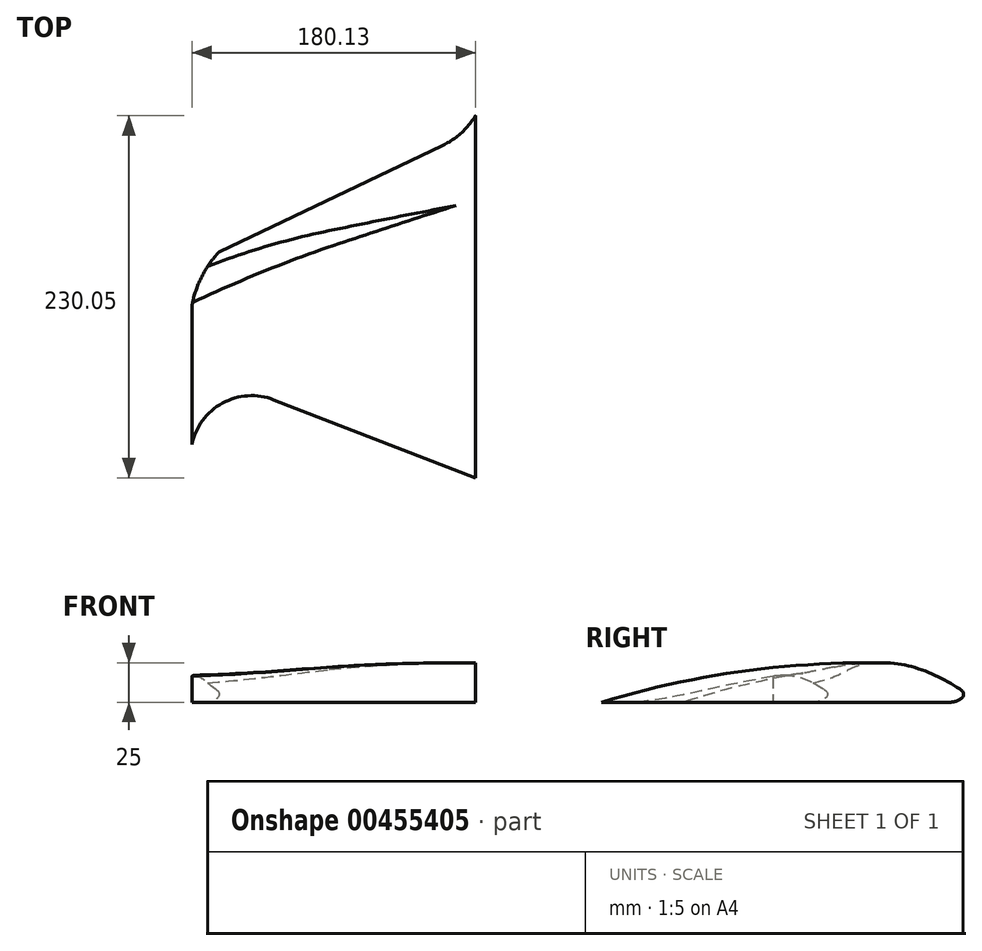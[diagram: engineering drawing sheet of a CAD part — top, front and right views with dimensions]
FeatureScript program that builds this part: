
annotation { "Feature Type Name" : "Feature", "Feature Type Description" : "" }
export const myFeature = defineFeature(function(context is Context, id is Id, definition is map)
    precondition{}
    {
        {
            var Q0;
            Q0=qCreatedBy(makeId("Top.planeOp"),FACE);
            var sketch = newSketch(context, id + "F0", { "sketchPlane" : qUnion([Q0])});
            skLineSegment(sketch, "E0", {"start": v(35.75, 56.99) * mm, "end": v(-84, 0) * mm});
            skArc(sketch, "E1", {"start": v(-84, 0) * mm, "mid": v(-108.74, -20.11) * mm, "end": v(-121.49, -49.34) * mm});
            skLineSegment(sketch, "E2", {"start": v(-121.49, -137.07) * mm, "end": v(-121.49, -49.34) * mm});
            skPoint(sketch, "E3.end.orphan", {"position": v(-24.95, -49.34) * mm});
            skArc(sketch, "E4", {"start": v(35.75, 56.99) * mm, "mid": v(49.78, 67.5) * mm, "end": v(58.64, 82.63) * mm});
            skLineSegment(sketch, "E5", {"start": v(58.64, -158.26) * mm, "end": v(58.64, 82.63) * mm});
            skLineSegment(sketch, "E6", {"start": v(-69.44, -108.67) * mm, "end": v(58.64, -158.26) * mm});
            skArc(sketch, "E7", {"start": v(-69.44, -108.67) * mm, "mid": v(-102.05, -110.8) * mm, "end": v(-121.49, -137.07) * mm});
            skSolve(sketch);
        }
        {
            var Q0;
            Q0=makeQuery(id+"F0.imprint","IMPRINT",FACE,{"disambiguationData":[TD([[makeQuery(id+"F0.imprint","IMPRINT",EDGE,{"derivedFrom":sQuery(id+"F0.wireOp",EDGE,"E0")}),1.0]])]});
            extrude(context, id + "F1", {"entities" : qUnion([Q0]), "depth" : 25 * mm});
        }
        {
            var Q0;
            Q0=makeQuery(id+"F1.opExtrude","CAP_EDGE",EDGE,{"disambiguationData":[OSD([sQuery(id+"F0.wireOp",EDGE,"E1")])],"isStart":false});
            fillet(context, id + "F2", {"entities" : qUnion([Q0]), "radius" : 48.84 * mm, "tangentPropagation" : true, "allowEdgeOverflow" : false});
        }
        {
            var Q0;
            Q0=makeQuery(id+"F1.opExtrude","CAP_EDGE",EDGE,{"disambiguationData":[OSD([sQuery(id+"F0.wireOp",EDGE,"3242a47b-ee2a-40f1-a814-2dec62063a9a")])],"isStart":false});
            var Q1;
            Q1=makeQuery(id+"F1.opExtrude","CAP_EDGE",EDGE,{"disambiguationData":[OSD([sQuery(id+"F0.wireOp",EDGE,"E6")])],"isStart":false});
            fillet(context, id + "F3", {"entities" : qUnion([Q0, Q1]), "radius" : 504.86 * mm, "tangentPropagation" : true, "allowEdgeOverflow" : false});
        }
        {
            var Q0;
            {var subQ0=sQuery(id+"F0.wireOp",EDGE,"E0");Q0=makeQuery(id+"F2.opFillet","BLEND_EDGE",EDGE,{"blendedFrom":[makeQuery(id+"F1.opExtrude","CAP_EDGE",EDGE,{"disambiguationData":[OSD([subQ0])],"isStart":false}),makeQuery(id+"F1.opExtrude","CAP_FACE",FACE,{"disambiguationData":[OSD([subQ0,sQuery(id+"F0.wireOp",EDGE,"E1"),sQuery(id+"F0.wireOp",EDGE,"E2"),sQuery(id+"F0.wireOp",EDGE,"E4"),sQuery(id+"F0.wireOp",EDGE,"E5"),sQuery(id+"F0.wireOp",EDGE,"E6"),sQuery(id+"F0.wireOp",EDGE,"3242a47b-ee2a-40f1-a814-2dec62063a9a")])],"isStart":true})],"blendedInto":[makeQuery(id+"F1.opExtrude","CAP_FACE",FACE,{"disambiguationData":[OSD([subQ0,sQuery(id+"F0.wireOp",EDGE,"E1"),sQuery(id+"F0.wireOp",EDGE,"E2"),sQuery(id+"F0.wireOp",EDGE,"E4"),sQuery(id+"F0.wireOp",EDGE,"E5"),sQuery(id+"F0.wireOp",EDGE,"E6"),sQuery(id+"F0.wireOp",EDGE,"3242a47b-ee2a-40f1-a814-2dec62063a9a")])],"isStart":true})]});}
            fillet(context, id + "F4", {"entities" : qUnion([Q0]), "radius" : 5 * mm, "tangentPropagation" : true, "allowEdgeOverflow" : false});
        }
        {
            var Q0;
            Q0=makeQuery(id+"F3.opFillet","BLEND_EDGE",EDGE,{"blendedFrom":[makeQuery(id+"F1.opExtrude","CAP_EDGE",EDGE,{"disambiguationData":[OSD([sQuery(id+"F0.wireOp",EDGE,"E6")])],"isStart":false}),makeQuery(id+"F2.opFillet","BLEND_FACE",FACE,{"disambiguationData":[OSD([sQuery(id+"F0.wireOp",EDGE,"E0")])]})],"blendedInto":[makeQuery(id+"F2.opFillet","BLEND_FACE",FACE,{"disambiguationData":[OSD([sQuery(id+"F0.wireOp",EDGE,"E0")])]})]});
            var Q1;
            Q1=makeQuery(id+"F3.opFillet","BLEND_EDGE",EDGE,{"blendedFrom":[makeQuery(id+"F1.opExtrude","CAP_EDGE",EDGE,{"disambiguationData":[OSD([sQuery(id+"F0.wireOp",EDGE,"E7")])],"isStart":false}),makeQuery(id+"F2.opFillet","BLEND_FACE",FACE,{"disambiguationData":[OSD([sQuery(id+"F0.wireOp",EDGE,"E0")])]})],"blendedInto":[makeQuery(id+"F2.opFillet","BLEND_FACE",FACE,{"disambiguationData":[OSD([sQuery(id+"F0.wireOp",EDGE,"E0")])]})]});
            fillet(context, id + "F5", {"entities" : qUnion([Q0, Q1]), "radius" : 20 * mm, "tangentPropagation" : true, "allowEdgeOverflow" : false});
        }
    });
